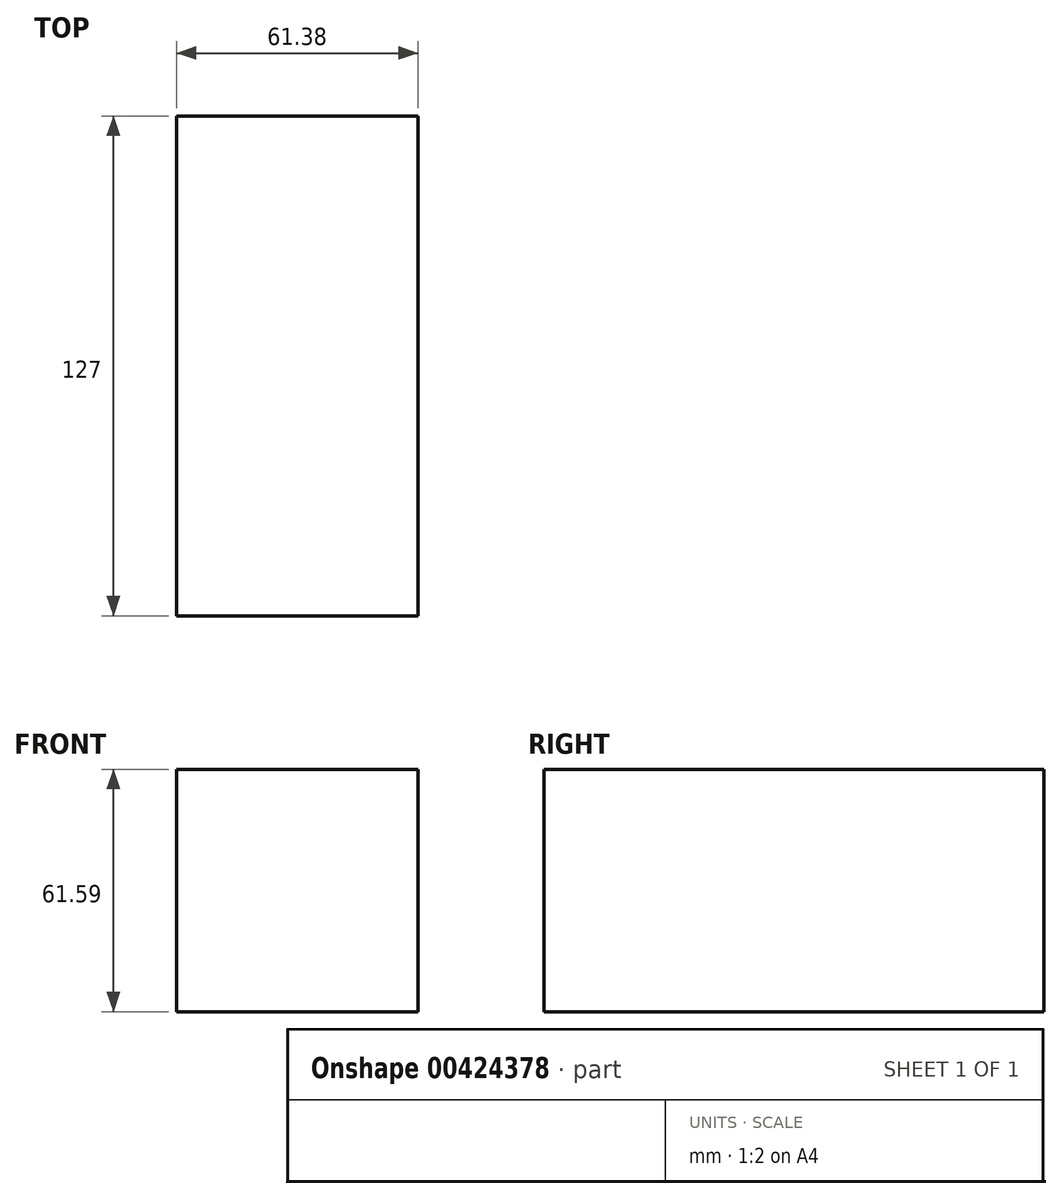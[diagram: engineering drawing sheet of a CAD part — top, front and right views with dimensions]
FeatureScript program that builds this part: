
annotation { "Feature Type Name" : "Feature", "Feature Type Description" : "" }
export const myFeature = defineFeature(function(context is Context, id is Id, definition is map)
    precondition{}
    {
        {
            var Q0;
            Q0=qCreatedBy(makeId("Front.planeOp"),FACE);
            var sketch = newSketch(context, id + "F0", { "sketchPlane" : qUnion([Q0])});
            skLineSegment(sketch, "E0.bottom", {"start": v(-41.9, 51.82) * mm, "end": v(-45.72, 51.82) * mm});
            skLineSegment(sketch, "E0.top", {"start": v(-41.9, 0) * mm, "end": v(-45.72, 0) * mm});
            skLineSegment(sketch, "E0.left", {"start": v(-41.9, 51.82) * mm, "end": v(-41.9, 0) * mm});
            skLineSegment(sketch, "E0.right", {"start": v(-45.72, 51.82) * mm, "end": v(-45.72, 0) * mm});
            skPoint(sketch, "E1.firstSnap0", {"position": v(-45.72, 25.91) * mm});
            skLineSegment(sketch, "E1.bottom", {"start": v(-20.74, 25.91) * mm, "end": v(40.64, 25.91) * mm});
            skLineSegment(sketch, "E1.top", {"start": v(-20.74, -35.68) * mm, "end": v(40.64, -35.68) * mm});
            skLineSegment(sketch, "E1.left", {"start": v(-20.74, 25.91) * mm, "end": v(-20.74, -35.68) * mm});
            skLineSegment(sketch, "E1.right", {"start": v(40.64, 25.91) * mm, "end": v(40.64, -35.68) * mm});
            skLineSegment(sketch, "E2.bottom", {"start": v(-126.58, -154.23) * mm, "end": v(-107.95, -154.23) * mm});
            skLineSegment(sketch, "E2.top", {"start": v(-126.58, -123.03) * mm, "end": v(-107.95, -123.03) * mm});
            skLineSegment(sketch, "E2.left", {"start": v(-126.58, -154.23) * mm, "end": v(-126.58, -123.03) * mm});
            skLineSegment(sketch, "E2.right", {"start": v(-107.95, -154.23) * mm, "end": v(-107.95, -123.03) * mm});
            skSolve(sketch);
        }
        {
            var Q0;
            Q0=makeQuery(id+"F0.imprint","IMPRINT",FACE,{"disambiguationData":[TD([[makeQuery(id+"F0.imprint","IMPRINT",EDGE,{"derivedFrom":sQuery(id+"F0.wireOp",EDGE,"E1.bottom")}),-1.0]])]});
            var sketch = newSketch(context, id + "F1", { "sketchPlane" : qUnion([Q0])});
            skSolve(sketch);
        }
        {
            var Q0;
            Q0=makeQuery(id+"F1.imprint","IMPRINT",FACE,{"disambiguationData":[TD([[makeQuery(id+"F1.imprint","IMPRINT",EDGE,{"derivedFrom":makeQuery(id+"F0.imprint","IMPRINT",EDGE,{"derivedFrom":sQuery(id+"F0.wireOp",EDGE,"E1.bottom")})}),-1.0]])]});
            extrude(context, id + "F2", {"entities" : qUnion([Q0]), "depth" : 127 * mm});
        }
    });
